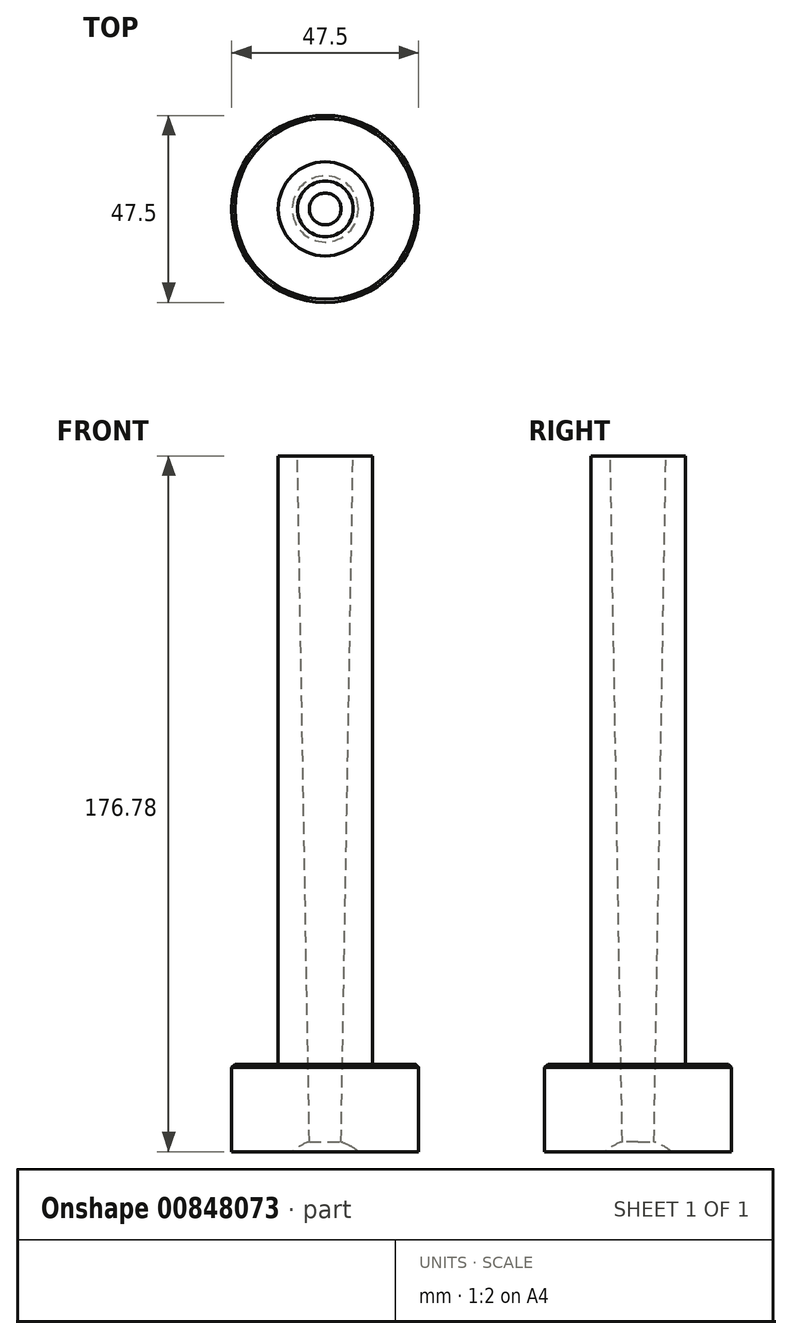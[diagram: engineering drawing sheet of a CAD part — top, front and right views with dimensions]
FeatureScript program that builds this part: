
annotation { "Feature Type Name" : "Feature", "Feature Type Description" : "" }
export const myFeature = defineFeature(function(context is Context, id is Id, definition is map)
    precondition{}
    {
        {
            var Q0;
            Q0=qCreatedBy(makeId("Top.planeOp"),FACE);
            var sketch = newSketch(context, id + "F0", { "sketchPlane" : qUnion([Q0])});
            skCircle(sketch, "E0", {"center": v(0, 0) * mm, "radius": 23.75 * mm});
            skSolve(sketch);
        }
        {
            var Q0;
            Q0=makeQuery(id+"F0.imprint","IMPRINT",FACE,{"disambiguationData":[TD([[makeQuery(id+"F0.imprint","IMPRINT",EDGE,{"derivedFrom":sQuery(id+"F0.wireOp",EDGE,"E0")}),1.0]])]});
            extrude(context, id + "F1", {"entities" : qUnion([Q0]), "depth" : 22.22 * mm, "offsetDistance" : 25.4 * mm});
        }
        {
            var Q0;
            Q0=qCreatedBy(makeId("Top.planeOp"),FACE);
            var sketch = newSketch(context, id + "F2", { "sketchPlane" : qUnion([Q0])});
            skCircle(sketch, "E1", {"center": v(0, 0) * mm, "radius": 11.96 * mm});
            skSolve(sketch);
        }
        {
            var Q0;
            Q0=makeQuery(id+"F2.imprint","IMPRINT",FACE,{"disambiguationData":[TD([[makeQuery(id+"F2.imprint","IMPRINT",EDGE,{"derivedFrom":sQuery(id+"F2.wireOp",EDGE,"E1")}),1.0]])]});
            extrude(context, id + "F3", {"entities" : qUnion([Q0]), "operationType" : NewBodyOperationType.ADD, "depth" : 176.78 * mm, "offsetDistance" : 25.4 * mm});
        }
        {
            var Q0;
            Q0=qCreatedBy(makeId("Top.planeOp"),FACE);
            var sketch = newSketch(context, id + "F4", { "sketchPlane" : qUnion([Q0])});
            skCircle(sketch, "E2", {"center": v(0, 0) * mm, "radius": 3.98 * mm});
            skSolve(sketch);
        }
        {
            var Q0;
            Q0=makeQuery(id+"F4.imprint","IMPRINT",FACE,{"disambiguationData":[TD([[makeQuery(id+"F4.imprint","IMPRINT",EDGE,{"derivedFrom":sQuery(id+"F4.wireOp",EDGE,"E2")}),1.0]])]});
            extrude(context, id + "F5", {"entities" : qUnion([Q0]), "operationType" : NewBodyOperationType.REMOVE, "endBound" : BoundingType.THROUGH_ALL, "depth" : 25.4 * mm, "offsetDistance" : 25.4 * mm, "hasDraft" : true, "draftAngle" : 1 * degree});
        }
        {
            var Q0;
            Q0=qCreatedBy(makeId("Front.planeOp"),FACE);
            var sketch = newSketch(context, id + "F6", { "sketchPlane" : qUnion([Q0])});
            skLineSegment(sketch, "E3", {"start": v(0, 0) * mm, "end": v(0, -9.53) * mm});
            skArc(sketch, "E4", {"start": v(0, 3.18) * mm, "mid": v(-12.7, -9.52) * mm, "end": v(0, -22.23) * mm});
            skLineSegment(sketch, "E5", {"start": v(0, 3.18) * mm, "end": v(0, -22.23) * mm});
            skSolve(sketch);
        }
        {
            var Q0;
            {var subQ0=sQuery(id+"F6.wireOp",EDGE,"E4");Q0=makeQuery(id+"F6.imprint","IMPRINT",FACE,{"disambiguationData":[TD([[makeQuery(id+"F6.imprint","IMPRINT",EDGE,{"derivedFrom":subQ0}),1.0]])]});}
            var Q1;
            Q1=sQuery(id+"F6.wireOp",EDGE,"E3");
            revolve(context, id + "F7", {"operationType" : NewBodyOperationType.REMOVE, "surfaceOperationType" : NewSurfaceOperationType.NEW, "entities" : qUnion([Q0]), "axis" : qUnion([Q1]), "revolveType" : RevolveType.ONE_DIRECTION, "oppositeDirection" : true, "angle" : 360 * degree});
        }
        {
            var Q0;
            Q0=makeQuery(id+"F1.opExtrude","CAP_EDGE",EDGE,{"disambiguationData":[OSD([sQuery(id+"F0.wireOp",EDGE,"E0")])],"isStart":false});
            chamfer(context, id + "F8", {"entities" : qUnion([Q0]), "width" : 0.79 * mm, "tangentPropagation" : true});
        }
    });
